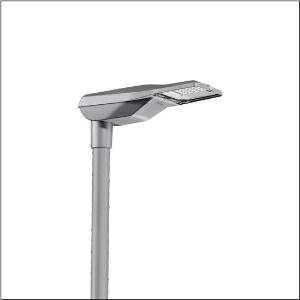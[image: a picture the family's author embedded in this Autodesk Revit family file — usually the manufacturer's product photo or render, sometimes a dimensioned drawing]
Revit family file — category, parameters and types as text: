
# Revit family: streetlight_sl_21_iq_micro___st1_0a_5xe1d41g08db_b7c0
name_source: partatom
category: Lighting Fixtures
units: mm (PartAtom-declared; Revit-internal decimal feet)

## family parameters
Cut with Voids When Loaded = No
Host = Face
Light Source = No
Part Type = Normal
Room Calculation Point = No
Round Connector Dimension = Use Diameter
Shared = No

## types (1)
- --- (1 x LED, 5010 lm, 36.4 W, 4000K)
    Apparent Load = 36 VA
    CIE Flux Codes = 37 72 97 100 100
    Color Rendering = 70
    Color Temperature = 4000K
    Default Elevation = 1800 mm
    Description = Streetlight SL 21 iQ micro, mast luminaire, primary light control with lens, of PMMA, primary optical cover: cover, of toughened safety glass, transparent, light distribution: ST1.0a, light emission: direct distribution, primary light characteristic: asymmetric, installation type: post-top, side-entry, LED, High Power LED, rated luminous flux: 5.010lm, luminous efficacy: 138lm/W, light colour: 740, colour temperature: 4000K, control: Street-Remote, Auto-Match, Temp-Guard, Lumen-Switch, Night-Set, Smart-Wire, Light-Fading, Desk-Remote (wireless, voltage-free reading and setting of iQ features in the workshop via application-optimized NFC function/RFID function), optimised constant luminous flux control (CLO 2.0), pre-setting: linear dimming characteristic, mains connection: 220..240V, AC, 50/60Hz, start of lifetime: 36W, end of service life: 38W, reduction: 16W, luminaire housing, of diecast aluminium, powder-coated, Siteco® metallic grey (DB 702S), corrosivity category C5 mid according to DIN EN ISO 12944, please order mast flange separately, inclination adjustable: 0°, 5°, 10°, 15°, sealing non-destructively replaceable, multi-level sealing system, length: 528mm, width: 235mm, height: 110mm, mast flange for spigot size: 42mm (side-entry): 5XC10008XM4, 60/48mm (side-entry/post-top): 5XC10108XM2, 76/60mm (side-entry/post-top): 5XC10108XM1, protection rating (complete): IP66, insulation class (complete): insulation class II (safety insulation), certification: CE, ENEC, ENEC+, VDE, impact resistance: IK09, permissible operating ambient temperature for outdoor applications: -40..+50°C, standard-compliant lighting for roads and squares, packaging unit: 1 piece

Light Distribution: ST1.0a
    Height = 110 mm
    Lamp = 1 x LED
    Lamp Light Flux = 5010 lm
    Lamp Power = 36.4 W
    Lamp count = 1
    Length = 528 mm
    Luminous efficacy = 138 lm/W
    Manufacturer = Siteco
    ModVariant = No
    Model = 5XE1D41G08DB
    Number of Poles = 1
    OnlyDefault = Yes
    Power Factor = 1
    Product Name = Streetlight SL 21 iQ micro | ST1.0a
    Product group = mast luminaire | pylon top
    ProductGroupID = 6100
    Protection Class = Protection class II
    Protection Degree = IP 66
    RLX_Detail_Level = 1
    RLX_Emergency_Light_Flux = 0 lm
    RLX_Emergency_Type = 0
    RLX_Emergency_Type_DB = No
    RlxData = <blob elided: 99477 chars, md5=bf9f3bdf>
    Socket = socket
    Standby Power = 0 W
    System Light Flux = 5010 lm
    System Power = 36 W
    Type Comments = factory setting: luminous flux: 100 % | dim-lin: 254 | 715 mA
    Type Image = l_1006881.jpg
    URL = http://relux.com
    VarID = @adj_126283
    Voltage = 0 V
    Weight = 0.00 kg
    Width = 235 mm

## geometry (parser evidence)
native form markers: Blend x4, Sweep x9
no freeform markers — native parametric forms only
